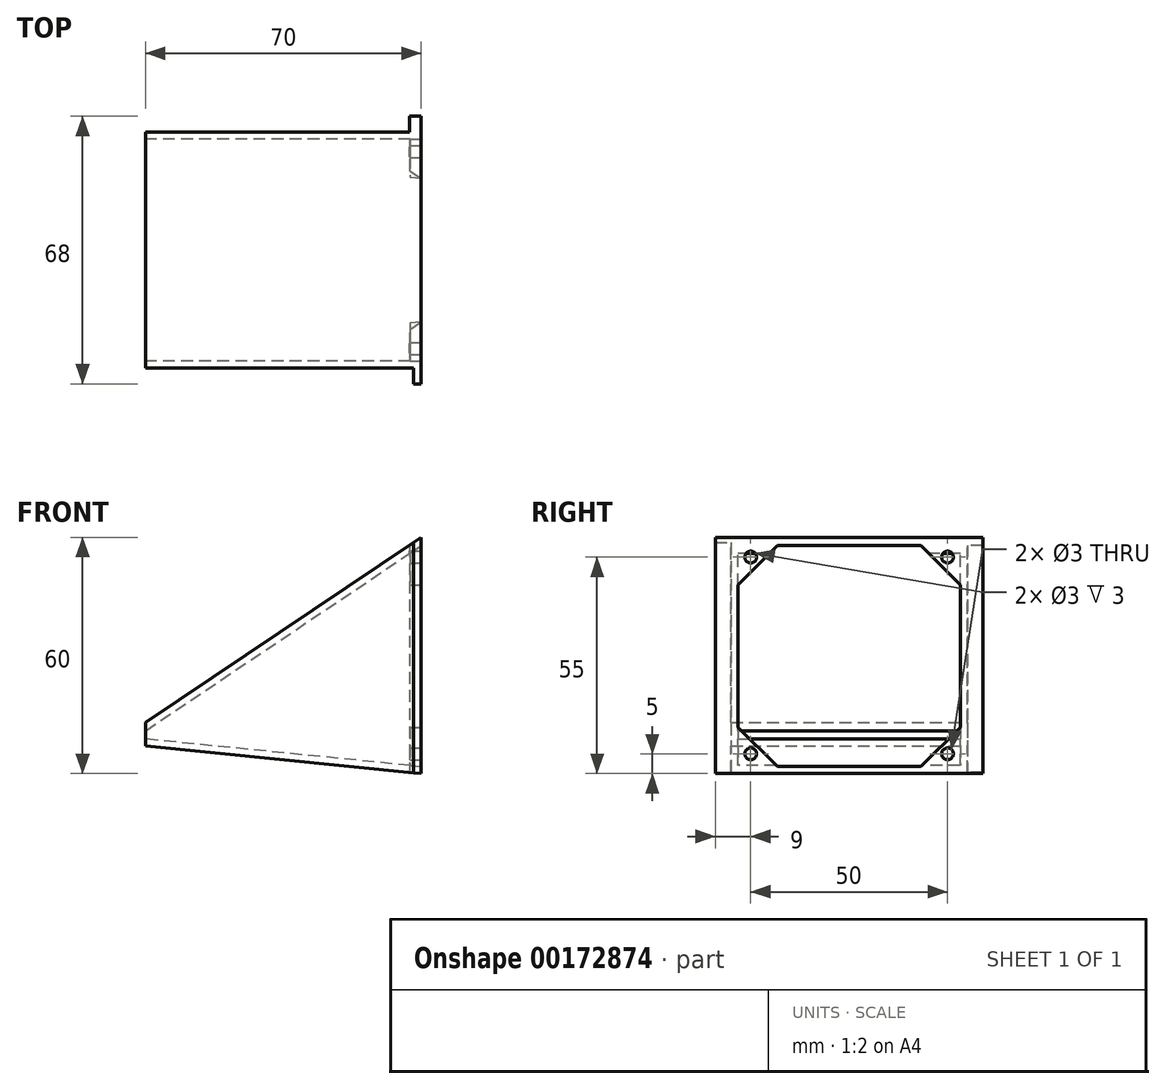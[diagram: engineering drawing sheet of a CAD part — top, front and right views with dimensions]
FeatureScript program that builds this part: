
annotation { "Feature Type Name" : "Feature", "Feature Type Description" : "" }
export const myFeature = defineFeature(function(context is Context, id is Id, definition is map)
    precondition{}
    {
        {
            var Q0;
            Q0=qCreatedBy(makeId("Front.planeOp"),FACE);
            var sketch = newSketch(context, id + "F0", { "sketchPlane" : qUnion([Q0])});
            skLineSegment(sketch, "E0", {"start": v(-70, 3) * mm, "end": v(-70, -3) * mm});
            skLineSegment(sketch, "E1", {"start": v(-70, 3) * mm, "end": v(0, 50) * mm});
            skLineSegment(sketch, "E2", {"start": v(0, 50) * mm, "end": v(0, -10) * mm});
            skLineSegment(sketch, "E3", {"start": v(0, -10) * mm, "end": v(-70, -3) * mm});
            skSolve(sketch);
        }
        {
            var Q0;
            Q0=makeQuery(id+"F0.imprint","IMPRINT",FACE,{"disambiguationData":[TD([[makeQuery(id+"F0.imprint","IMPRINT",EDGE,{"derivedFrom":sQuery(id+"F0.wireOp",EDGE,"E0")}),1.0]])]});
            extrude(context, id + "F1", {"entities" : qUnion([Q0]), "depth" : 60 * mm});
        }
        {
            var Q0;
            Q0=makeQuery(id+"F1.opExtrude","SWEPT_FACE",FACE,{"disambiguationData":[OSD([sQuery(id+"F0.wireOp",EDGE,"E2")])]});
            var Q1;
            Q1=makeQuery(id+"F1.opExtrude","SWEPT_FACE",FACE,{"disambiguationData":[OSD([sQuery(id+"F0.wireOp",EDGE,"E0")])]});
            shell(context, id + "F2", {"entities" : qUnion([Q0, Q1]), "thickness" : 1.75 * mm});
        }
        {
            var Q0;
            Q0=makeQuery(id+"F1.opExtrude","SWEPT_FACE",FACE,{"disambiguationData":[OSD([sQuery(id+"F0.wireOp",EDGE,"E2")])]});
            var sketch = newSketch(context, id + "F3", { "sketchPlane" : qUnion([Q0])});
            skLineSegment(sketch, "E4", {"start": v(-48.25, 47.9) * mm, "end": v(-58.25, 37.9) * mm});
            skLineSegment(sketch, "E5", {"start": v(-58.25, 37.9) * mm, "end": v(-58.25, 47.9) * mm});
            skLineSegment(sketch, "E6", {"start": v(-58.25, 47.9) * mm, "end": v(-48.25, 47.9) * mm});
            skLineSegment(sketch, "E7", {"start": v(-11.75, 47.9) * mm, "end": v(-1.75, 37.9) * mm});
            skLineSegment(sketch, "E8", {"start": v(-1.75, 37.9) * mm, "end": v(-1.75, 47.9) * mm});
            skLineSegment(sketch, "E9", {"start": v(-1.75, 47.9) * mm, "end": v(-11.75, 47.9) * mm});
            skLineSegment(sketch, "E10", {"start": v(-58.25, 1.76) * mm, "end": v(-48.25, -8.24) * mm});
            skLineSegment(sketch, "E11", {"start": v(-48.25, -8.24) * mm, "end": v(-58.25, -8.24) * mm});
            skLineSegment(sketch, "E12", {"start": v(-58.25, -8.24) * mm, "end": v(-58.25, 1.76) * mm});
            skLineSegment(sketch, "E13", {"start": v(-11.75, -8.24) * mm, "end": v(-1.75, 1.76) * mm});
            skLineSegment(sketch, "E14", {"start": v(-1.75, 1.76) * mm, "end": v(-1.75, -8.24) * mm});
            skLineSegment(sketch, "E15", {"start": v(-1.75, -8.24) * mm, "end": v(-11.75, -8.24) * mm});
            skSolve(sketch);
        }
        {
            var Q0;
            Q0 = qSketchRegion(id + "F3", true);
            extrude(context, id + "F4", {"entities" : qUnion([Q0]), "operationType" : NewBodyOperationType.ADD, "oppositeDirection" : true, "depth" : 2.8 * mm});
        }
        {
            var Q0;
            Q0=makeQuery(id+"F4.boolean.opBoolean","MERGE",FACE,{"derivedFrom":[makeQuery(id+"F1.opExtrude","SWEPT_FACE",FACE,{"disambiguationData":[OSD([sQuery(id+"F0.wireOp",EDGE,"E2")])]}),makeQuery(id+"F4.opExtrude","CAP_FACE",FACE,{"disambiguationData":[OSD([sQuery(id+"F3.wireOp",EDGE,"E4"),sQuery(id+"F3.wireOp",EDGE,"E5"),sQuery(id+"F3.wireOp",EDGE,"E6")])],"isStart":true}),makeQuery(id+"F4.opExtrude","CAP_FACE",FACE,{"disambiguationData":[OSD([sQuery(id+"F3.wireOp",EDGE,"E7"),sQuery(id+"F3.wireOp",EDGE,"E8"),sQuery(id+"F3.wireOp",EDGE,"E9")])],"isStart":true}),makeQuery(id+"F4.opExtrude","CAP_FACE",FACE,{"disambiguationData":[OSD([sQuery(id+"F3.wireOp",EDGE,"E10"),sQuery(id+"F3.wireOp",EDGE,"E11"),sQuery(id+"F3.wireOp",EDGE,"E12")])],"isStart":true}),makeQuery(id+"F4.opExtrude","CAP_FACE",FACE,{"disambiguationData":[OSD([sQuery(id+"F3.wireOp",EDGE,"E13"),sQuery(id+"F3.wireOp",EDGE,"E14"),sQuery(id+"F3.wireOp",EDGE,"E15")])],"isStart":true})]});
            var sketch = newSketch(context, id + "F5", { "sketchPlane" : qUnion([Q0])});
            skCircle(sketch, "E16", {"center": v(-55, 45) * mm, "radius": 1.5 * mm});
            skCircle(sketch, "E17", {"center": v(-5, 45) * mm, "radius": 1.5 * mm});
            skCircle(sketch, "E18", {"center": v(-55, -5) * mm, "radius": 1.5 * mm});
            skCircle(sketch, "E19", {"center": v(-5, -5) * mm, "radius": 1.5 * mm});
            skSolve(sketch);
        }
        {
            var Q0;
            Q0=makeQuery(id+"F5.imprint","IMPRINT",FACE,{"disambiguationData":[TD([[makeQuery(id+"F5.imprint","IMPRINT",EDGE,{"derivedFrom":sQuery(id+"F5.wireOp",EDGE,"E16")}),1.0]])]});
            var Q1;
            Q1=makeQuery(id+"F5.imprint","IMPRINT",FACE,{"disambiguationData":[TD([[makeQuery(id+"F5.imprint","IMPRINT",EDGE,{"derivedFrom":sQuery(id+"F5.wireOp",EDGE,"E17")}),1.0]])]});
            var Q2;
            Q2=makeQuery(id+"F5.imprint","IMPRINT",FACE,{"disambiguationData":[TD([[makeQuery(id+"F5.imprint","IMPRINT",EDGE,{"derivedFrom":sQuery(id+"F5.wireOp",EDGE,"E18")}),1.0]])]});
            var Q3;
            Q3=makeQuery(id+"F5.imprint","IMPRINT",FACE,{"disambiguationData":[TD([[makeQuery(id+"F5.imprint","IMPRINT",EDGE,{"derivedFrom":sQuery(id+"F5.wireOp",EDGE,"E19")}),1.0]])]});
            extrude(context, id + "F6", {"entities" : qUnion([Q0, Q1, Q2, Q3]), "operationType" : NewBodyOperationType.REMOVE, "oppositeDirection" : true, "depth" : 3 * mm});
        }
        {
            var Q0;
            Q0=makeQuery(id+"F1.opExtrude","CAP_FACE",FACE,{"disambiguationData":[OSD([sQuery(id+"F0.wireOp",EDGE,"E0"),sQuery(id+"F0.wireOp",EDGE,"E1"),sQuery(id+"F0.wireOp",EDGE,"E2"),sQuery(id+"F0.wireOp",EDGE,"E3")])],"isStart":false});
            var sketch = newSketch(context, id + "F7", { "sketchPlane" : qUnion([Q0])});
            skLineSegment(sketch, "E20", {"start": v(-2, 48.66) * mm, "end": v(-2, -9.8) * mm});
            skSolve(sketch);
        }
        {
            var Q0;
            {var subQ0=sQuery(id+"F7.wireOp",EDGE,"E20");Q0=makeQuery(id+"F7.imprint","IMPRINT",FACE,{"disambiguationData":[TD([[makeQuery(id+"F7.imprint","IMPRINT",EDGE,{"derivedFrom":subQ0}),1.0]])]});}
            extrude(context, id + "F8", {"entities" : qUnion([Q0]), "operationType" : NewBodyOperationType.ADD, "depth" : 4 * mm});
        }
        {
            var Q0;
            Q0=makeQuery(id+"F1.opExtrude","CAP_FACE",FACE,{"disambiguationData":[OSD([sQuery(id+"F0.wireOp",EDGE,"E0"),sQuery(id+"F0.wireOp",EDGE,"E1"),sQuery(id+"F0.wireOp",EDGE,"E2"),sQuery(id+"F0.wireOp",EDGE,"E3")])],"isStart":true});
            var sketch = newSketch(context, id + "F9", { "sketchPlane" : qUnion([Q0])});
            skLineSegment(sketch, "E21", {"start": v(2.99, 48) * mm, "end": v(2.99, -9.7) * mm});
            skSolve(sketch);
        }
        {
            var Q0;
            {var subQ0=sQuery(id+"F9.wireOp",EDGE,"E21");Q0=makeQuery(id+"F9.imprint","IMPRINT",FACE,{"disambiguationData":[TD([[makeQuery(id+"F9.imprint","IMPRINT",EDGE,{"derivedFrom":subQ0}),-1.0]])]});}
            extrude(context, id + "F10", {"entities" : qUnion([Q0]), "operationType" : NewBodyOperationType.ADD, "depth" : 4 * mm});
        }
    });
